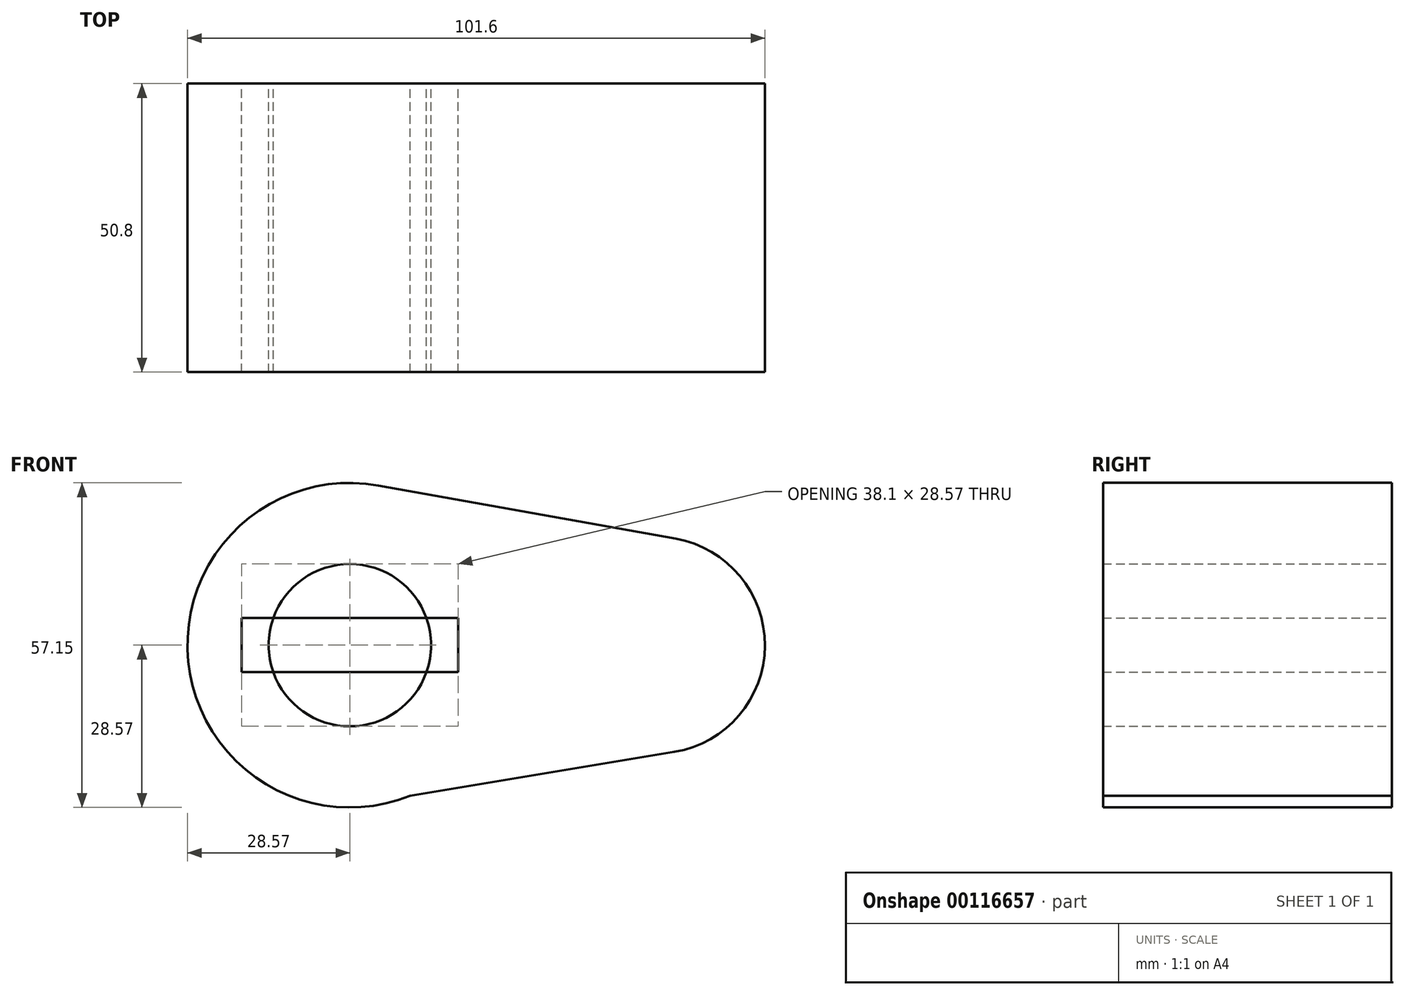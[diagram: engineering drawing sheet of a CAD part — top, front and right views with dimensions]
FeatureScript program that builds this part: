
annotation { "Feature Type Name" : "Feature", "Feature Type Description" : "" }
export const myFeature = defineFeature(function(context is Context, id is Id, definition is map)
    precondition{}
    {
        {
            var Q0;
            Q0=qCreatedBy(makeId("Front.planeOp"),FACE);
            var sketch = newSketch(context, id + "F0", { "sketchPlane" : qUnion([Q0])});
            skCircle(sketch, "E0", {"center": v(0, 0) * mm, "radius": 28.57 * mm});
            skCircle(sketch, "E1", {"center": v(53.98, 0) * mm, "radius": 19.05 * mm});
            skLineSegment(sketch, "E2", {"start": v(5.04, 28.13) * mm, "end": v(57.34, 18.75) * mm});
            skLineSegment(sketch, "E3", {"start": v(10.6, -26.54) * mm, "end": v(57.1, -18.8) * mm});
            skCircle(sketch, "E4", {"center": v(0, 0) * mm, "radius": 14.29 * mm});
            skCircle(sketch, "E5", {"center": v(53.98, 0) * mm, "radius": 14.29 * mm});
            skLineSegment(sketch, "E6.bottom", {"start": v(-19.05, -4.76) * mm, "end": v(19.05, -4.76) * mm});
            skLineSegment(sketch, "E6.top", {"start": v(-19.05, 4.76) * mm, "end": v(19.05, 4.76) * mm});
            skLineSegment(sketch, "E6.left", {"start": v(-19.05, -4.76) * mm, "end": v(-19.05, 4.76) * mm});
            skLineSegment(sketch, "E6.right", {"start": v(19.05, -4.76) * mm, "end": v(19.05, 4.76) * mm});
            skSolve(sketch);
        }
        {
            var Q0;
            Q0 = qSketchRegion(id + "F0", true);
            extrude(context, id + "F1", {"entities" : qUnion([Q0]), "depth" : 25.4 * mm});
        }
        {
            var Q0;
            {var subQ11=sQuery(id+"F0.wireOp",EDGE,"E6.left");Q0=makeQuery(id+"F0.imprint","IMPRINT",FACE,{"disambiguationData":[TD([[makeQuery(id+"F0.imprint","IMPRINT",EDGE,{"derivedFrom":subQ11}),1.0]])]});}
            var Q1;
            Q1=makeQuery(id+"F0.imprint","IMPRINT",FACE,{"disambiguationData":[TD([[makeQuery(id+"F0.imprint","IMPRINT",EDGE,{"derivedFrom":sQuery(id+"F0.wireOp",EDGE,"E5")}),1.0]])]});
            var Q2;
            Q2=makeQuery(id+"F0.imprint","IMPRINT",FACE,{"disambiguationData":[TD([[makeQuery(id+"F0.imprint","IMPRINT",EDGE,{"derivedFrom":sQuery(id+"F0.wireOp",EDGE,"E5")}),-1.0]])]});
            var Q3;
            {var subQ0=sQuery(id+"F0.wireOp",EDGE,"E2");Q3=makeQuery(id+"F0.imprint","IMPRINT",FACE,{"disambiguationData":[TD([[makeQuery(id+"F0.imprint","IMPRINT",EDGE,{"derivedFrom":subQ0}),-1.0]])]});}
            var Q4;
            {var subQ0=sQuery(id+"F0.wireOp",EDGE,"E6.top");var subQ1=sQuery(id+"F0.wireOp",EDGE,"E4");var subQ2=makeQuery(id+"F0.imprint","INTERSECT",VERTEX,{"disambiguationData":[OD(0.0)],"derivedFrom":[subQ1,subQ0]});Q4=makeQuery(id+"F0.imprint","IMPRINT",FACE,{"disambiguationData":[TD([[makeQuery(id+"F0.imprint","IMPRINT",EDGE,{"disambiguationData":[TD([[subQ2,-1.0]])],"derivedFrom":subQ1}),1.0]])]});}
            extrude(context, id + "F2", {"entities" : qUnion([Q0, Q1, Q2, Q3, Q4]), "operationType" : NewBodyOperationType.ADD, "depth" : 50.8 * mm});
        }
    });
